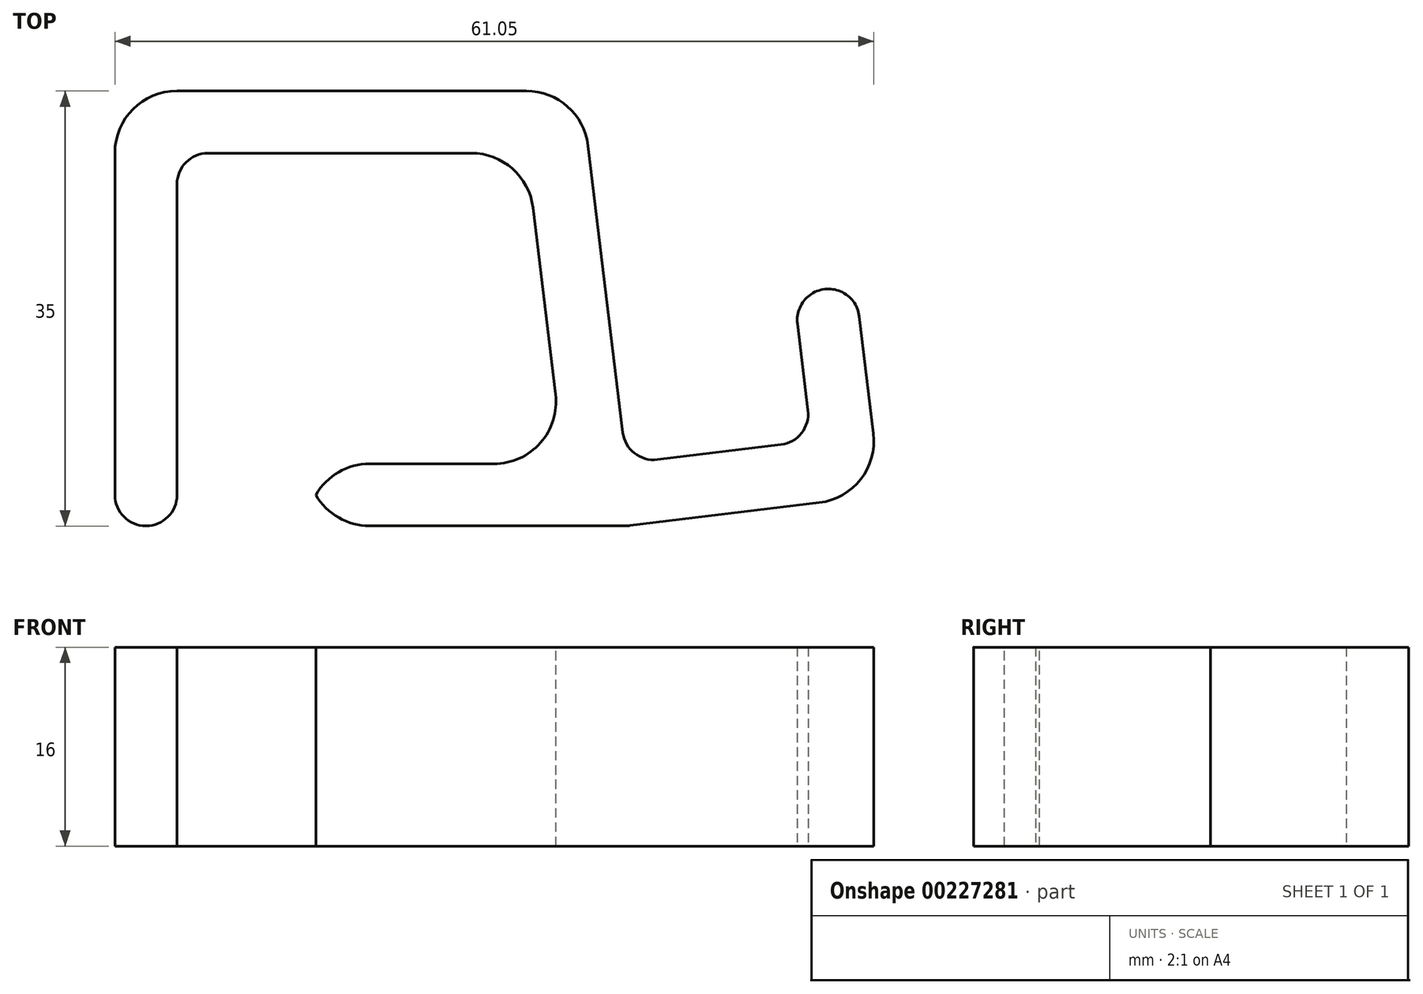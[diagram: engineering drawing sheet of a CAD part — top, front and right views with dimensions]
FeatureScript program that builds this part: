
annotation { "Feature Type Name" : "Feature", "Feature Type Description" : "" }
export const myFeature = defineFeature(function(context is Context, id is Id, definition is map)
    precondition{}
    {
        {
            var Q0;
            Q0=qCreatedBy(makeId("Top.planeOp"),FACE);
            var sketch = newSketch(context, id + "F0", { "sketchPlane" : qUnion([Q0])});
            skLineSegment(sketch, "E0.bottom", {"start": v(-15.5, -104.19) * mm, "end": v(-10.5, -104.19) * mm});
            skLineSegment(sketch, "E0.top", {"start": v(-15.5, -134.19) * mm, "end": v(-10.5, -134.19) * mm});
            skLineSegment(sketch, "E0.left", {"start": v(-15.5, -104.19) * mm, "end": v(-15.5, -134.19) * mm});
            skLineSegment(sketch, "E0.right", {"start": v(-10.5, -104.19) * mm, "end": v(-10.5, -134.19) * mm});
            skLineSegment(sketch, "E1.bottom", {"start": v(-15.5, -104.19) * mm, "end": v(0, -104.19) * mm});
            skLineSegment(sketch, "E1.top", {"start": v(-15.5, -99.19) * mm, "end": v(0, -99.19) * mm});
            skLineSegment(sketch, "E1.left", {"start": v(-15.5, -104.19) * mm, "end": v(-15.5, -99.19) * mm});
            skLineSegment(sketch, "E1.right", {"start": v(0, -104.19) * mm, "end": v(0, -99.19) * mm});
            skLineSegment(sketch, "E2.bottom", {"start": v(0, -104.19) * mm, "end": v(-5, -104.19) * mm});
            skLineSegment(sketch, "E2.top", {"start": v(0, -134.19) * mm, "end": v(-5, -134.19) * mm});
            skLineSegment(sketch, "E2.left", {"start": v(0, -104.19) * mm, "end": v(0, -134.19) * mm});
            skLineSegment(sketch, "E2.right", {"start": v(-5, -104.19) * mm, "end": v(-5, -134.19) * mm});
            skLineSegment(sketch, "E3", {"start": v(-5, -47.23) * mm, "end": v(-5, 75.67) * mm, "construction": true});
            skLineSegment(sketch, "E4.left", {"start": v(0, -134.19) * mm, "end": v(0, -129.19) * mm});
            skLineSegment(sketch, "E5", {"start": v(39.1, -115.43) * mm, "end": v(40.55, -127.35) * mm});
            skLineSegment(sketch, "E6", {"start": v(22.03, -99.19) * mm, "end": v(0, -99.19) * mm});
            skLineSegment(sketch, "E7", {"start": v(22.03, -99.19) * mm, "end": v(25.66, -129.15) * mm});
            skLineSegment(sketch, "E8", {"start": v(20.62, -129.19) * mm, "end": v(17.6, -104.19) * mm});
            skLineSegment(sketch, "E9", {"start": v(17.6, -104.19) * mm, "end": v(0, -104.19) * mm});
            skLineSegment(sketch, "E10", {"start": v(25.66, -129.15) * mm, "end": v(40.55, -127.35) * mm});
            skLineSegment(sketch, "E11", {"start": v(25.66, -134.19) * mm, "end": v(46.11, -131.7) * mm});
            skLineSegment(sketch, "E12", {"start": v(0, -134.19) * mm, "end": v(25.66, -134.19) * mm});
            skLineSegment(sketch, "E13", {"start": v(0, -129.19) * mm, "end": v(20.62, -129.19) * mm});
            skLineSegment(sketch, "E14", {"start": v(0, 207.49) * mm, "end": v(-5, 206.88) * mm});
            skLineSegment(sketch, "E15", {"start": v(25.66, -129.15) * mm, "end": v(-5, 124) * mm});
            skLineSegment(sketch, "E16", {"start": v(40.51, -61.2) * mm, "end": v(32.65, -62.15) * mm});
            skLineSegment(sketch, "E17", {"start": v(39.1, -115.43) * mm, "end": v(44.07, -114.83) * mm});
            skLineSegment(sketch, "E18", {"start": v(44.07, -114.83) * mm, "end": v(46.11, -131.7) * mm});
            skSolve(sketch);
        }
        {
            var Q0;
            Q0=makeQuery(id+"F0.imprint","IMPRINT",FACE,{"disambiguationData":[TD([[makeQuery(id+"F0.imprint","IMPRINT",EDGE,{"derivedFrom":sQuery(id+"F0.wireOp",EDGE,"E0.top")}),1.0]])]});
            var Q1;
            Q1=makeQuery(id+"F0.imprint","IMPRINT",FACE,{"disambiguationData":[TD([[makeQuery(id+"F0.imprint","IMPRINT",EDGE,{"derivedFrom":sQuery(id+"F0.wireOp",EDGE,"E1.top")}),-1.0]])]});
            var Q2;
            Q2=makeQuery(id+"F0.imprint","IMPRINT",FACE,{"disambiguationData":[TD([[makeQuery(id+"F0.imprint","IMPRINT",EDGE,{"derivedFrom":sQuery(id+"F0.wireOp",EDGE,"E2.bottom")}),1.0]])]});
            var Q3;
            Q3=makeQuery(id+"F0.imprint","IMPRINT",FACE,{"disambiguationData":[TD([[makeQuery(id+"F0.imprint","IMPRINT",EDGE,{"derivedFrom":sQuery(id+"F0.wireOp",EDGE,"E1.right")}),-1.0]])]});
            extrude(context, id + "F1", {"entities" : qUnion([Q0, Q1, Q2, Q3]), "depth" : 16 * mm});
        }
        {
            var Q0;
            Q0=makeQuery(id+"F1.opExtrude","SWEPT_EDGE",EDGE,{"disambiguationData":[OSD([sQuery(id+"F0.wireOp",EDGE,"E1.top"),sQuery(id+"F0.wireOp",EDGE,"E1.left")])]});
            var Q1;
            Q1=makeQuery(id+"F1.opExtrude","SWEPT_EDGE",EDGE,{"disambiguationData":[OSD([sQuery(id+"F0.wireOp",EDGE,"M8ddDKvl-P1wp-dwZk-o0P2-siRPg5FdM426"),sQuery(id+"F0.wireOp",EDGE,"lwqNqyqY-Rap4-XfkX-i2UZ-jy8pZGiPETUf")])]});
            var Q2;
            Q2=makeQuery(id+"F1.opExtrude","SWEPT_EDGE",EDGE,{"disambiguationData":[OSD([sQuery(id+"F0.wireOp",EDGE,"E11"),sQuery(id+"F0.wireOp",EDGE,"lwqNqyqY-Rap4-XfkX-i2UZ-jy8pZGiPETUf")])]});
            var Q3;
            Q3=makeQuery(id+"F1.opExtrude","SWEPT_EDGE",EDGE,{"disambiguationData":[OSD([sQuery(id+"F0.wireOp",EDGE,"E1.right"),sQuery(id+"F0.wireOp",EDGE,"E2.bottom"),sQuery(id+"F0.wireOp",EDGE,"E2.left"),sQuery(id+"F0.wireOp",EDGE,"E9")])]});
            var Q4;
            Q4=makeQuery(id+"F1.opExtrude","SWEPT_EDGE",EDGE,{"disambiguationData":[OSD([sQuery(id+"F0.wireOp",EDGE,"E8"),sQuery(id+"F0.wireOp",EDGE,"E9")])]});
            var Q5;
            Q5=makeQuery(id+"F1.opExtrude","SWEPT_EDGE",EDGE,{"disambiguationData":[OSD([sQuery(id+"F0.wireOp",EDGE,"E8"),sQuery(id+"F0.wireOp",EDGE,"E13")])]});
            var Q6;
            Q6=makeQuery(id+"F1.opExtrude","SWEPT_EDGE",EDGE,{"disambiguationData":[OSD([sQuery(id+"F0.wireOp",EDGE,"E2.left"),sQuery(id+"F0.wireOp",EDGE,"E4.left"),sQuery(id+"F0.wireOp",EDGE,"E13")])]});
            var Q7;
            Q7=makeQuery(id+"F1.opExtrude","SWEPT_EDGE",EDGE,{"disambiguationData":[OSD([sQuery(id+"F0.wireOp",EDGE,"E2.top"),sQuery(id+"F0.wireOp",EDGE,"E2.right")])]});
            var Q8;
            Q8=makeQuery(id+"F1.opExtrude","SWEPT_EDGE",EDGE,{"disambiguationData":[OSD([sQuery(id+"F0.wireOp",EDGE,"E6"),sQuery(id+"F0.wireOp",EDGE,"E15")])]});
            fillet(context, id + "F2", {"entities" : qUnion([Q0, Q1, Q2, Q3, Q4, Q5, Q6, Q7, Q8]), "radius" : 5 * mm, "tangentPropagation" : true, "allowEdgeOverflow" : false});
        }
        {
            var Q0;
            Q0=makeQuery(id+"F1.opExtrude","SWEPT_EDGE",EDGE,{"disambiguationData":[OSD([sQuery(id+"F0.wireOp",EDGE,"E17"),sQuery(id+"F0.wireOp",EDGE,"E18")])]});
            var Q1;
            Q1=makeQuery(id+"F1.opExtrude","SWEPT_EDGE",EDGE,{"disambiguationData":[OSD([sQuery(id+"F0.wireOp",EDGE,"E5"),sQuery(id+"F0.wireOp",EDGE,"E17")])]});
            var Q2;
            Q2=makeQuery(id+"F1.opExtrude","SWEPT_EDGE",EDGE,{"disambiguationData":[OSD([sQuery(id+"F0.wireOp",EDGE,"E0.top"),sQuery(id+"F0.wireOp",EDGE,"E0.left")])]});
            var Q3;
            Q3=makeQuery(id+"F1.opExtrude","SWEPT_EDGE",EDGE,{"disambiguationData":[OSD([sQuery(id+"F0.wireOp",EDGE,"E0.top"),sQuery(id+"F0.wireOp",EDGE,"E0.right")])]});
            var Q4;
            Q4=makeQuery(id+"F1.opExtrude","SWEPT_EDGE",EDGE,{"disambiguationData":[OSD([sQuery(id+"F0.wireOp",EDGE,"E0.right"),sQuery(id+"F0.wireOp",EDGE,"E1.bottom")])]});
            var Q5;
            Q5=makeQuery(id+"F1.opExtrude","SWEPT_EDGE",EDGE,{"disambiguationData":[OSD([sQuery(id+"F0.wireOp",EDGE,"E1.bottom"),sQuery(id+"F0.wireOp",EDGE,"E2.bottom"),sQuery(id+"F0.wireOp",EDGE,"E2.right")])]});
            var Q6;
            Q6=makeQuery(id+"F1.opExtrude","SWEPT_EDGE",EDGE,{"disambiguationData":[OSD([sQuery(id+"F0.wireOp",EDGE,"E10"),sQuery(id+"F0.wireOp",EDGE,"E15")])]});
            var Q7;
            Q7=makeQuery(id+"F1.opExtrude","SWEPT_EDGE",EDGE,{"disambiguationData":[OSD([sQuery(id+"F0.wireOp",EDGE,"E5"),sQuery(id+"F0.wireOp",EDGE,"E10")])]});
            fillet(context, id + "F3", {"entities" : qUnion([Q0, Q1, Q2, Q3, Q4, Q5, Q6, Q7]), "radius" : 2.5 * mm, "tangentPropagation" : true, "allowEdgeOverflow" : false});
        }
    });
